# Revit family: CADS_AIRFLOWdev_AirTerminal_DoubleAirBrick_Exhaust
name_source: partatom
category: Air Terminals
revit_build: Autodesk Revit 2015 (Build: 20160512_0715(x64)
units: mm (PartAtom-declared; Revit-internal decimal feet)

## types (3) — shared parameters
6MonthlyMaintenance = Visually inspect system, clean the fan and ducting if necessary
AirflowRateRange = 0-61
AssetType = Fixed
CEApproval = Yes
Default Elevation = 1219 mm
DurationUnit = Years
Exclusions = Incorrect Use / Incorrect Installation / Installed by a non-accredited electrician. Customer abuse.
FaceType = LOUVERED
Finish = Matte
FlowControlType = NONE
Grade = Virgin
GrossWeight = 0.02 kg
H = 155 mm
HasIntegralControl = No
HasSoundAttenuator = No
HasThermalInsulation = No
ISO140001 = Yes
ISO90001 = Yes
IsExtendedWarranty = No
L = 235 mm  [stored 0.770997 ft]
Manufacturer = Airflow Developments Ltd
ManufacturerAddress = Aidelle House
Lancaster Road
Cressex Business Park
High Wycombe
Bucks
HP123QP
ManufacturerTelephone = 01494 525252
ManufacturerWebsite = www.airflow.com
Material = Plastic
MountingType = FLATFLUSH
NBSCode = 90-75-50/370 Air terminals;
NominalHeight = 145 mm  [stored 0.475722 ft]
NominalLength = 80 mm  [stored 0.262467 ft]
NominalWidth = 245 mm  [stored 0.803806 ft]
NumberOfSlots = 44
PointOfContact = Airflow Developments Ltd
ProductionYear = 2017
ReplacementCost = 52.416
ServiceLifeDuration = 10
ServiceLifeType = EXPECTEDSERVICELIFE
Shape = Rectangular
ShippingWeight = 0.02 kg
Size = 80 x 245 x 145
Uniclass2015 = Pr_65_70_46_01
W = 140 mm  [stored 0.459318 ft]
WarrantyContent = Replacement of part if faulty
WarrantyGuarantor = Airflow Developments Ltd
WarrantyPeriod = 2

## per-type parameters (varying)
| type | Color | Constituents | Description | Double_AirBrick | GlobalTradeItemNumber | ModelLabel | ModelReference |
| Terracotta | Terracotta | Terracotta | 204 x 60mm Double Airbrick duct adaptor (Terracotta) | CADS_AirFlow_Terracotta | 5019009308944 | 204 x 60mm Double Airbrick duct adaptor (Terracotta) | 90000077 |
| White | White | White | 204 x 60mm Double Airbrick duct adaptor (White) | CADS_AirFlow_White | 5019009308937 | 204 x 60mm Double Airbrick duct adaptor (White) | 90000076 |
| Stone | Costwold Stone | Costwold Stone | 204 x 60mm Double Airbrick duct adaptor (Cotswold Stone) | CADS_AirFlow_Stone | 5019009310404 | 204 x 60mm Double Airbrick duct adaptor (Cotswold Stone) | 90000132 |

note: [stored X ft] marks values corroborated as IEEE doubles in the binary element streams (Revit-internal decimal feet)

## geometry (parser evidence)
native form markers: Blend x4, Sweep x2
no freeform markers — native parametric forms only
